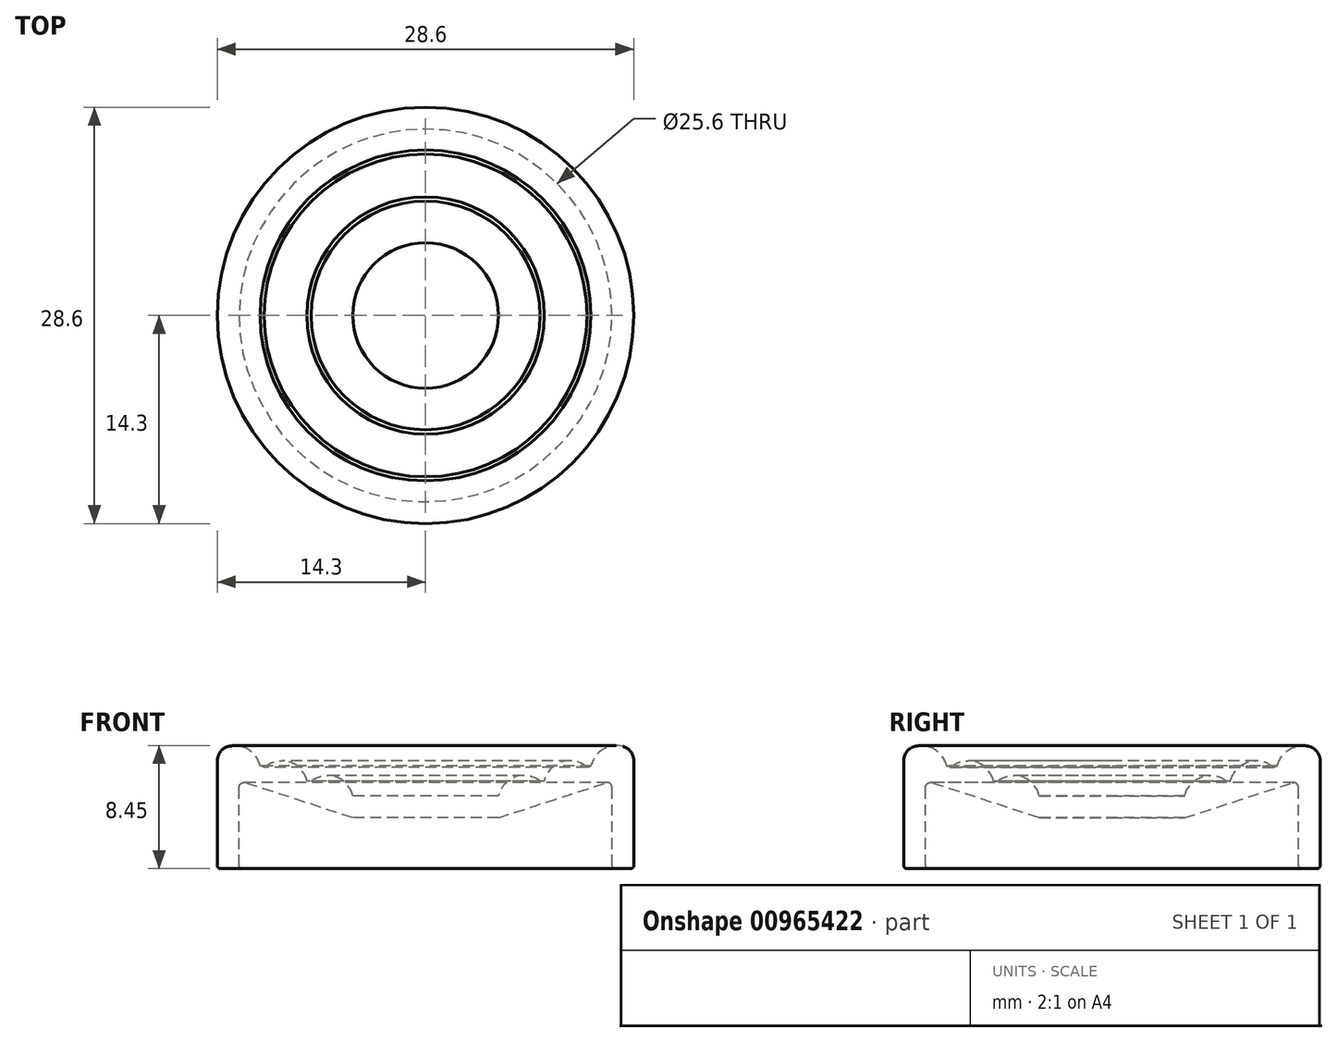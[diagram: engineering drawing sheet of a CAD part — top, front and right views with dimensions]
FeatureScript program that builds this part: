
annotation { "Feature Type Name" : "Feature", "Feature Type Description" : "" }
export const myFeature = defineFeature(function(context is Context, id is Id, definition is map)
    precondition{}
    {
        {
            var Q0;
            Q0=qCreatedBy(makeId("Front.planeOp"),FACE);
            var sketch = newSketch(context, id + "F0", { "sketchPlane" : qUnion([Q0])});
            skLineSegment(sketch, "E0.right", {"start": v(-14.3, 0) * mm, "end": v(-14.3, 8) * mm});
            skLineSegment(sketch, "E1", {"start": v(-14.3, 8) * mm, "end": v(-5, 5) * mm, "construction": true});
            skLineSegment(sketch, "E2", {"start": v(-5, 5) * mm, "end": v(0, 5) * mm});
            skLineSegment(sketch, "E3", {"start": v(0, 5) * mm, "end": v(0, 3.5) * mm});
            skArc(sketch, "E4", {"start": v(-11.36, 7.05) * mm, "mid": v(-12.56, 8.36) * mm, "end": v(-14.3, 8) * mm});
            skArc(sketch, "E5", {"start": v(-8.15, 6.02) * mm, "mid": v(-9.35, 7.32) * mm, "end": v(-11.08, 6.96) * mm});
            skArc(sketch, "E6", {"start": v(-5, 5) * mm, "mid": v(-6.15, 6.29) * mm, "end": v(-7.85, 6.02) * mm});
            skLineSegment(sketch, "E7", {"start": v(-14.3, 7.03) * mm, "end": v(0, 2.42) * mm, "construction": true});
            skLineSegment(sketch, "E8", {"start": v(-12.8, 0) * mm, "end": v(-12.8, 0.11) * mm});
            skLineSegment(sketch, "E9", {"start": v(-12.4, 5.89) * mm, "end": v(-5, 3.5) * mm});
            skLineSegment(sketch, "E10", {"start": v(-5, 3.5) * mm, "end": v(0, 3.5) * mm});
            skPoint(sketch, "E11.visualSharp", {"position": v(-12.8, 6.02) * mm});
            skArc(sketch, "E11.filletArc", {"start": v(-12.4, 5.89) * mm, "mid": v(-12.68, 5.85) * mm, "end": v(-12.8, 5.6) * mm});
            skLineSegment(sketch, "E12", {"start": v(-12.8, 0.11) * mm, "end": v(-12.8, 5.6) * mm});
            skLineSegment(sketch, "E13", {"start": v(0, 3.5) * mm, "end": v(0, 3.5) * mm});
            skLineSegment(sketch, "E14", {"start": v(-12.8, 0) * mm, "end": v(-14.3, 0) * mm});
            skLineSegment(sketch, "E15", {"start": v(-11.36, 7.05) * mm, "end": v(-11.08, 6.96) * mm});
            skLineSegment(sketch, "E16", {"start": v(-7.85, 6.02) * mm, "end": v(-8.15, 6.02) * mm});
            skSolve(sketch);
        }
        {
            var Q0;
            {var subQ2=sQuery(id+"F0.wireOp",EDGE,"E0.right");Q0=makeQuery(id+"F0.imprint","IMPRINT",FACE,{"disambiguationData":[TD([[makeQuery(id+"F0.imprint","IMPRINT",EDGE,{"derivedFrom":subQ2}),-1.0]])]});}
            var Q1;
            Q1=sQuery(id+"F0.wireOp",EDGE,"E3");
            revolve(context, id + "F1", {"surfaceOperationType" : NewSurfaceOperationType.NEW, "entities" : qUnion([Q0]), "axis" : qUnion([Q1]), "revolveType" : RevolveType.FULL});
        }
        {
            var Q0;
            Q0=makeQuery(id+"F1.opRevolve","SWEPT_EDGE",EDGE,{"disambiguationData":[OSD([sQuery(id+"F0.wireOp",EDGE,"E0.right"),sQuery(id+"F0.wireOp",EDGE,"E4")])]});
            fillet(context, id + "F2", {"entities" : qUnion([Q0]), "radius" : 1 * mm, "allowEdgeOverflow" : false});
        }
        {
            var Q0;
            Q0=makeQuery(id+"F1.opRevolve","SWEPT_EDGE",EDGE,{"disambiguationData":[OSD([sQuery(id+"F0.wireOp",EDGE,"E0.right"),sQuery(id+"F0.wireOp",EDGE,"E14")])]});
            fillet(context, id + "F3", {"entities" : qUnion([Q0]), "radius" : 0.2 * mm, "tangentPropagation" : true, "allowEdgeOverflow" : false});
        }
        {
            var Q0;
            Q0=makeQuery(id+"F1.opRevolve","SWEPT_EDGE",EDGE,{"disambiguationData":[OSD([sQuery(id+"F0.wireOp",EDGE,"E8"),sQuery(id+"F0.wireOp",EDGE,"E14")])]});
            fillet(context, id + "F4", {"entities" : qUnion([Q0]), "radius" : 0.2 * mm, "tangentPropagation" : true, "allowEdgeOverflow" : false});
        }
    });
